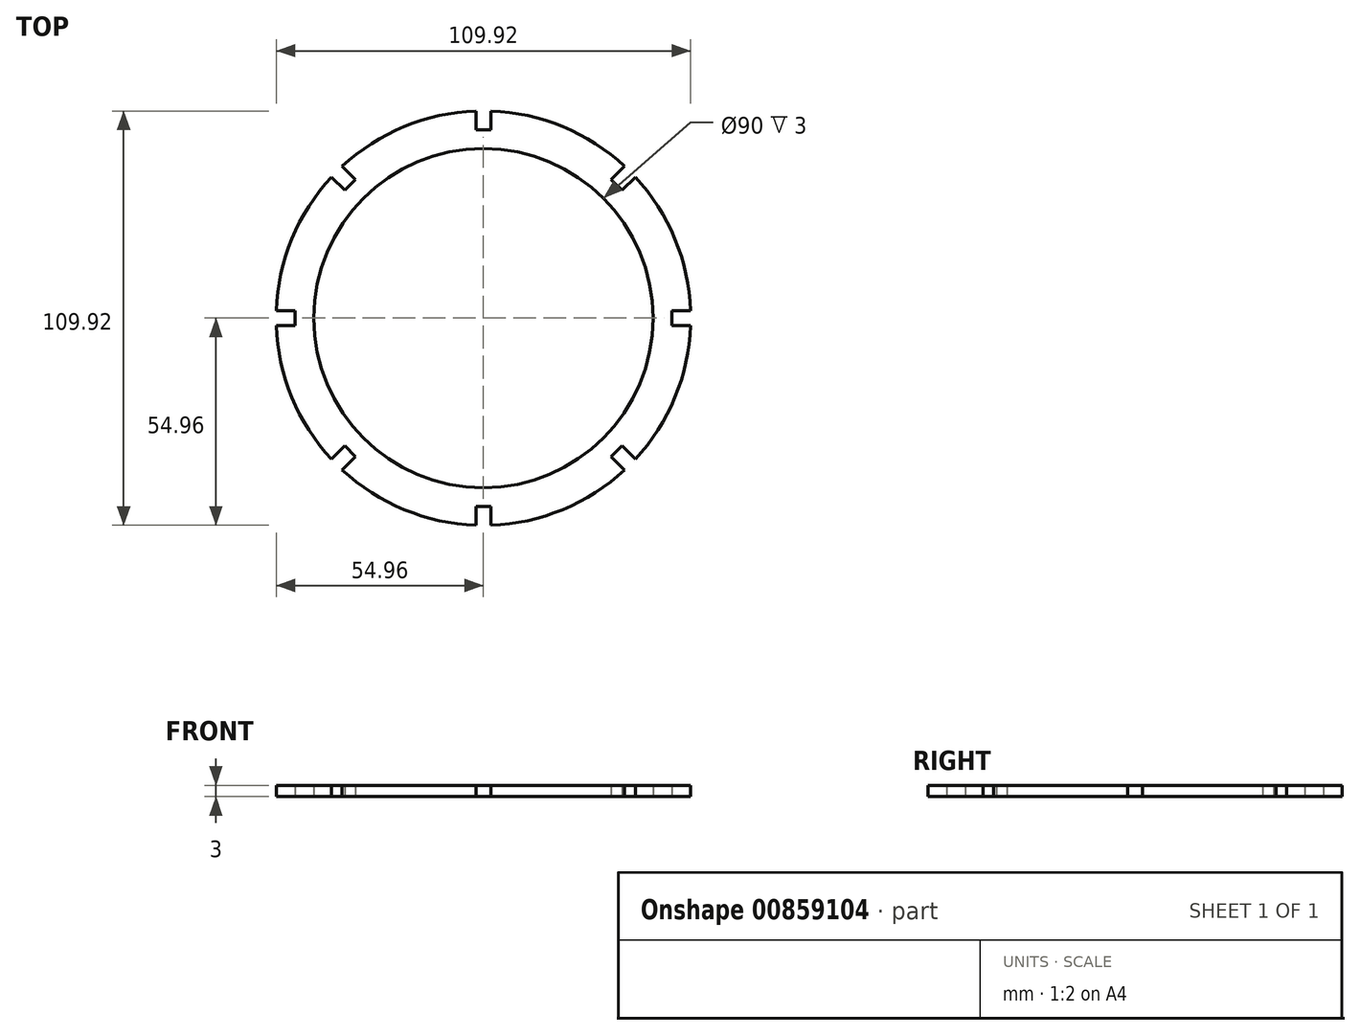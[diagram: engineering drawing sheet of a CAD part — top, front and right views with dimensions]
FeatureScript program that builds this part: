
annotation { "Feature Type Name" : "Feature", "Feature Type Description" : "" }
export const myFeature = defineFeature(function(context is Context, id is Id, definition is map)
    precondition{}
    {
        {
            var Q0;
            Q0=qCreatedBy(makeId("Top.planeOp"),FACE);
            var sketch = newSketch(context, id + "F0", { "sketchPlane" : qUnion([Q0])});
            skCircle(sketch, "E0", {"center": v(0, 0) * mm, "radius": 55 * mm});
            skCircle(sketch, "E1", {"center": v(0, 0) * mm, "radius": 45 * mm});
            skLineSegment(sketch, "E2", {"start": v(0, -49.96) * mm, "end": v(2, -49.96) * mm});
            skLineSegment(sketch, "E3", {"start": v(2, -49.96) * mm, "end": v(-2, -49.96) * mm});
            skLineSegment(sketch, "E4", {"start": v(-2, -49.96) * mm, "end": v(-2, -54.96) * mm});
            skLineSegment(sketch, "E5", {"start": v(2, -49.96) * mm, "end": v(2, -54.96) * mm});
            skLineSegment(sketch, "E6.1.0", {"start": v(33.92, -36.74) * mm, "end": v(37.45, -40.28) * mm});
            skLineSegment(sketch, "E6.1.1", {"start": v(36.74, -33.92) * mm, "end": v(33.92, -36.74) * mm});
            skLineSegment(sketch, "E6.1.2", {"start": v(36.74, -33.92) * mm, "end": v(40.28, -37.45) * mm});
            skLineSegment(sketch, "E6.2.0", {"start": v(49.96, -2) * mm, "end": v(54.96, -2) * mm});
            skLineSegment(sketch, "E6.2.1", {"start": v(49.96, 2) * mm, "end": v(49.96, -2) * mm});
            skLineSegment(sketch, "E6.2.2", {"start": v(49.96, 2) * mm, "end": v(54.96, 2) * mm});
            skLineSegment(sketch, "E6.3.0", {"start": v(36.74, 33.92) * mm, "end": v(40.28, 37.45) * mm});
            skLineSegment(sketch, "E6.3.1", {"start": v(33.92, 36.74) * mm, "end": v(36.74, 33.92) * mm});
            skLineSegment(sketch, "E6.3.2", {"start": v(33.92, 36.74) * mm, "end": v(37.45, 40.28) * mm});
            skLineSegment(sketch, "E6.4.0", {"start": v(2, 49.96) * mm, "end": v(2, 54.96) * mm});
            skLineSegment(sketch, "E6.4.1", {"start": v(-2, 49.96) * mm, "end": v(2, 49.96) * mm});
            skLineSegment(sketch, "E6.4.2", {"start": v(-2, 49.96) * mm, "end": v(-2, 54.96) * mm});
            skLineSegment(sketch, "E6.5.0", {"start": v(-33.92, 36.74) * mm, "end": v(-37.45, 40.28) * mm});
            skLineSegment(sketch, "E6.5.1", {"start": v(-36.74, 33.92) * mm, "end": v(-33.92, 36.74) * mm});
            skLineSegment(sketch, "E6.5.2", {"start": v(-36.74, 33.92) * mm, "end": v(-40.28, 37.45) * mm});
            skLineSegment(sketch, "E6.6.0", {"start": v(-49.96, 2) * mm, "end": v(-54.96, 2) * mm});
            skLineSegment(sketch, "E6.6.1", {"start": v(-49.96, -2) * mm, "end": v(-49.96, 2) * mm});
            skLineSegment(sketch, "E6.6.2", {"start": v(-49.96, -2) * mm, "end": v(-54.96, -2) * mm});
            skLineSegment(sketch, "E6.7.0", {"start": v(-36.74, -33.92) * mm, "end": v(-40.28, -37.45) * mm});
            skLineSegment(sketch, "E6.7.1", {"start": v(-33.92, -36.74) * mm, "end": v(-36.74, -33.92) * mm});
            skLineSegment(sketch, "E6.7.2", {"start": v(-33.92, -36.74) * mm, "end": v(-37.45, -40.28) * mm});
            skSolve(sketch);
        }
        {
            var Q0;
            Q0=makeQuery(id+"F0.imprint","IMPRINT",FACE,{"disambiguationData":[TD([[makeQuery(id+"F0.imprint","IMPRINT",EDGE,{"derivedFrom":sQuery(id+"F0.wireOp",EDGE,"E1")}),-1.0]])]});
            extrude(context, id + "F1", {"entities" : qUnion([Q0]), "depth" : 3 * mm, "offsetDistance" : 25 * mm});
        }
    });
